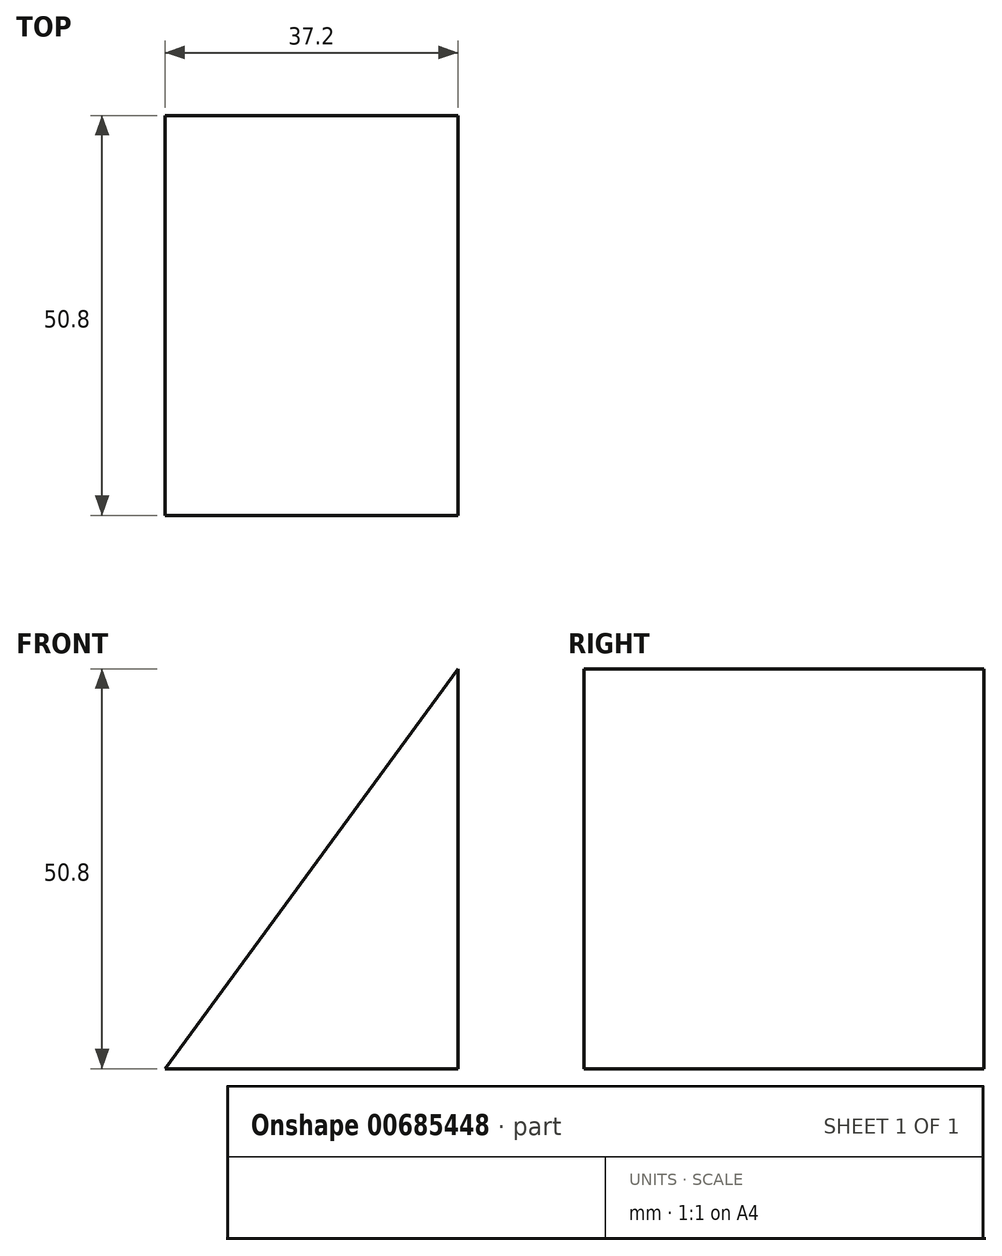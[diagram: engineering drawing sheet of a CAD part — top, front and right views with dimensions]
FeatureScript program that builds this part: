
annotation { "Feature Type Name" : "Feature", "Feature Type Description" : "" }
export const myFeature = defineFeature(function(context is Context, id is Id, definition is map)
    precondition{}
    {
        {
            var Q0;
            Q0=qCreatedBy(makeId("Front.planeOp"),FACE);
            var sketch = newSketch(context, id + "F0", { "sketchPlane" : qUnion([Q0])});
            skLineSegment(sketch, "E0", {"start": v(0, 0) * mm, "end": v(0, 50.8) * mm});
            skLineSegment(sketch, "E1", {"start": v(0, 50.8) * mm, "end": v(-37.2, 0) * mm});
            skLineSegment(sketch, "E2", {"start": v(-37.2, 0) * mm, "end": v(0, 0) * mm});
            skSolve(sketch);
        }
        {
            var Q0;
            Q0 = qSketchRegion(id + "F0", true);
            extrude(context, id + "F1", {"entities" : qUnion([Q0]), "depth" : 50.8 * mm, "offsetDistance" : 25.4 * mm});
        }
    });
